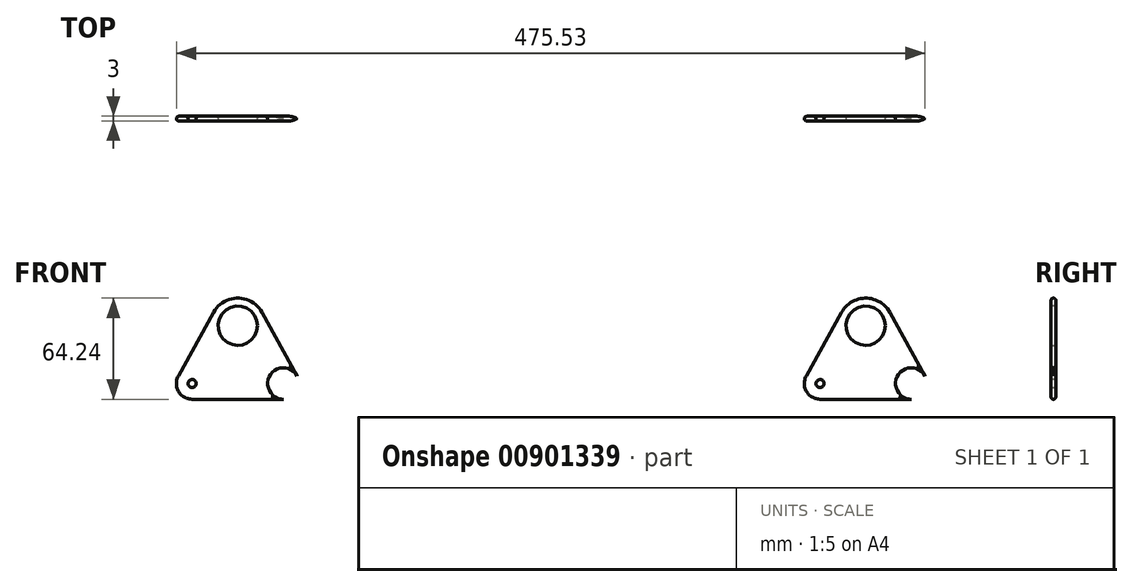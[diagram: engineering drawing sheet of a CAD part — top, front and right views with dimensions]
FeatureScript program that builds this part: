
annotation { "Feature Type Name" : "Feature", "Feature Type Description" : "" }
export const myFeature = defineFeature(function(context is Context, id is Id, definition is map)
    precondition{}
    {
        {
            var Q0;
            Q0=qCreatedBy(makeId("Front.planeOp"),FACE);
            var sketch = newSketch(context, id + "F0", { "sketchPlane" : qUnion([Q0])});
            skLineSegment(sketch, "E0", {"start": v(-199.41, 0) * mm, "end": v(-199.41, 45) * mm});
            skCircle(sketch, "E1", {"center": v(-199.41, 45) * mm, "radius": 17.5 * mm});
            skLineSegment(sketch, "E2", {"start": v(-199.41, 0) * mm, "end": v(-199.41, -45) * mm});
            skLineSegment(sketch, "E3", {"start": v(-199.41, -45) * mm, "end": v(-269.41, -45) * mm});
            skLineSegment(sketch, "E4", {"start": v(-199.41, -45) * mm, "end": v(-129.41, -45) * mm});
            skLineSegment(sketch, "E5", {"start": v(-129.41, -45) * mm, "end": v(-184.11, 53.5) * mm});
            skLineSegment(sketch, "E6", {"start": v(-269.41, -45) * mm, "end": v(-214.71, 53.5) * mm});
            skCircle(sketch, "E7", {"center": v(-239.67, -27.5) * mm, "radius": 17.5 * mm});
            skCircle(sketch, "E8", {"center": v(-159.15, -27.5) * mm, "radius": 17.5 * mm});
            skLineSegment(sketch, "E9", {"start": v(199.41, 0) * mm, "end": v(199.41, 45) * mm});
            skCircle(sketch, "E10", {"center": v(199.41, 45) * mm, "radius": 17.5 * mm});
            skLineSegment(sketch, "E11", {"start": v(199.41, 0) * mm, "end": v(199.41, -45) * mm});
            skLineSegment(sketch, "E12", {"start": v(199.41, -45) * mm, "end": v(129.41, -45) * mm});
            skLineSegment(sketch, "E13", {"start": v(199.41, -45) * mm, "end": v(269.41, -45) * mm});
            skLineSegment(sketch, "E14", {"start": v(269.41, -45) * mm, "end": v(214.71, 53.5) * mm});
            skLineSegment(sketch, "E15", {"start": v(129.41, -45) * mm, "end": v(184.11, 53.5) * mm});
            skCircle(sketch, "E16", {"center": v(159.15, -27.5) * mm, "radius": 17.5 * mm});
            skCircle(sketch, "E17", {"center": v(239.67, -27.5) * mm, "radius": 17.5 * mm});
            skCircle(sketch, "E18", {"center": v(-199.41, 45) * mm, "radius": 12.5 * mm});
            skCircle(sketch, "E19", {"center": v(199.41, 45) * mm, "radius": 12.5 * mm});
            skCircle(sketch, "E20", {"center": v(-228.4, 8.26) * mm, "radius": 10 * mm});
            skCircle(sketch, "E21.MirrorC", {"center": v(-170.43, 8.26) * mm, "radius": 10 * mm});
            skCircle(sketch, "E22.MirrorC", {"center": v(228.4, 8.26) * mm, "radius": 10 * mm});
            skCircle(sketch, "E23.MirrorC", {"center": v(170.43, 8.26) * mm, "radius": 10 * mm});
            skLineSegment(sketch, "E24", {"start": v(-228.4, -1.74) * mm, "end": v(-170.43, -1.74) * mm});
            skLineSegment(sketch, "E25.MirrorCS", {"start": v(228.4, -1.74) * mm, "end": v(170.43, -1.74) * mm});
            skCircle(sketch, "E26", {"center": v(-228.4, 8.26) * mm, "radius": 2.5 * mm});
            skCircle(sketch, "E27", {"center": v(-170.43, 8.26) * mm, "radius": 2.5 * mm});
            skCircle(sketch, "E28.MirrorC", {"center": v(170.43, 8.26) * mm, "radius": 2.5 * mm});
            skCircle(sketch, "E29.MirrorC", {"center": v(228.4, 8.26) * mm, "radius": 2.5 * mm});
            skLineSegment(sketch, "E30", {"start": v(-228.4, -1.74) * mm, "end": v(-199.41, -1.74) * mm});
            skSolve(sketch);
        }
        {
            var Q0;
            {var subQ0=sQuery(id+"F0.wireOp",EDGE,"E2");var subQ1=sQuery(id+"F0.wireOp",EDGE,"E0");var subQ2=makeQuery(id+"F0.imprint","INTERSECT",VERTEX,{"derivedFrom":[subQ1,subQ0]});Q0=makeQuery(id+"F0.imprint","IMPRINT",FACE,{"disambiguationData":[TD([[makeQuery(id+"F0.imprint","IMPRINT",EDGE,{"disambiguationData":[TD([[subQ2,-1.0]])],"derivedFrom":subQ1}),1.0]])]});}
            var Q1;
            Q1=makeQuery(id+"F0.imprint","IMPRINT",FACE,{"disambiguationData":[TD([[makeQuery(id+"F0.imprint","IMPRINT",EDGE,{"derivedFrom":sQuery(id+"F0.wireOp",EDGE,"E18")}),-1.0]])]});
            var Q2;
            {var subQ7=sQuery(id+"F0.wireOp",EDGE,"E2");var subQ8=sQuery(id+"F0.wireOp",EDGE,"E0");var subQ9=makeQuery(id+"F0.imprint","INTERSECT",VERTEX,{"derivedFrom":[subQ8,subQ7]});Q2=makeQuery(id+"F0.imprint","IMPRINT",FACE,{"disambiguationData":[TD([[makeQuery(id+"F0.imprint","IMPRINT",EDGE,{"disambiguationData":[TD([[subQ9,-1.0]])],"derivedFrom":subQ8}),-1.0]])]});}
            var Q3;
            {var subQ0=sQuery(id+"F0.wireOp",EDGE,"E11");var subQ1=sQuery(id+"F0.wireOp",EDGE,"E9");var subQ2=makeQuery(id+"F0.imprint","INTERSECT",VERTEX,{"derivedFrom":[subQ1,subQ0]});Q3=makeQuery(id+"F0.imprint","IMPRINT",FACE,{"disambiguationData":[TD([[makeQuery(id+"F0.imprint","IMPRINT",EDGE,{"disambiguationData":[TD([[subQ2,-1.0]])],"derivedFrom":subQ1}),1.0]])]});}
            var Q4;
            Q4=makeQuery(id+"F0.imprint","IMPRINT",FACE,{"disambiguationData":[TD([[makeQuery(id+"F0.imprint","IMPRINT",EDGE,{"derivedFrom":sQuery(id+"F0.wireOp",EDGE,"E19")}),-1.0]])]});
            var Q5;
            {var subQ5=sQuery(id+"F0.wireOp",EDGE,"E11");var subQ6=sQuery(id+"F0.wireOp",EDGE,"E9");var subQ7=makeQuery(id+"F0.imprint","INTERSECT",VERTEX,{"derivedFrom":[subQ6,subQ5]});Q5=makeQuery(id+"F0.imprint","IMPRINT",FACE,{"disambiguationData":[TD([[makeQuery(id+"F0.imprint","IMPRINT",EDGE,{"disambiguationData":[TD([[subQ7,-1.0]])],"derivedFrom":subQ6}),-1.0]])]});}
            var Q6;
            {var subQ0=sQuery(id+"F0.wireOp",EDGE,"E20");var subQ1=makeQuery(id+"F0.imprint","INTERSECT",VERTEX,{"derivedFrom":[subQ0,sQuery(id+"F0.wireOp",EDGE,"E24")]});Q6=makeQuery(id+"F0.imprint","IMPRINT",FACE,{"disambiguationData":[TD([[makeQuery(id+"F0.imprint","IMPRINT",EDGE,{"disambiguationData":[TD([[subQ1,1.0]])],"derivedFrom":subQ0}),1.0]])]});}
            var Q7;
            {var subQ0=sQuery(id+"F0.wireOp",EDGE,"E21.MirrorC");var subQ1=makeQuery(id+"F0.imprint","INTERSECT",VERTEX,{"derivedFrom":[subQ0,sQuery(id+"F0.wireOp",EDGE,"E24")]});Q7=makeQuery(id+"F0.imprint","IMPRINT",FACE,{"disambiguationData":[TD([[makeQuery(id+"F0.imprint","IMPRINT",EDGE,{"disambiguationData":[TD([[subQ1,1.0]])],"derivedFrom":subQ0}),-1.0]])]});}
            var Q8;
            {var subQ0=sQuery(id+"F0.wireOp",EDGE,"E23.MirrorC");var subQ1=makeQuery(id+"F0.imprint","INTERSECT",VERTEX,{"derivedFrom":[subQ0,sQuery(id+"F0.wireOp",EDGE,"E25.MirrorCS")]});Q8=makeQuery(id+"F0.imprint","IMPRINT",FACE,{"disambiguationData":[TD([[makeQuery(id+"F0.imprint","IMPRINT",EDGE,{"disambiguationData":[TD([[subQ1,1.0]])],"derivedFrom":subQ0}),1.0]])]});}
            var Q9;
            {var subQ0=sQuery(id+"F0.wireOp",EDGE,"E22.MirrorC");var subQ1=makeQuery(id+"F0.imprint","INTERSECT",VERTEX,{"derivedFrom":[subQ0,sQuery(id+"F0.wireOp",EDGE,"E25.MirrorCS")]});Q9=makeQuery(id+"F0.imprint","IMPRINT",FACE,{"disambiguationData":[TD([[makeQuery(id+"F0.imprint","IMPRINT",EDGE,{"disambiguationData":[TD([[subQ1,1.0]])],"derivedFrom":subQ0}),-1.0]])]});}
            extrude(context, id + "F1", {"entities" : qUnion([Q0, Q1, Q2, Q3, Q4, Q5, Q6, Q7, Q8, Q9]), "endBound" : BoundingType.SYMMETRIC, "depth" : 3 * mm, "offsetDistance" : 25 * mm});
        }
        {
            var Q0;
            Q0=makeQuery(id+"F1.opExtrude","CAP_FACE",FACE,{"disambiguationData":[OSD([sQuery(id+"F0.wireOp",EDGE,"E1"),sQuery(id+"F0.wireOp",EDGE,"E3"),sQuery(id+"F0.wireOp",EDGE,"E4"),sQuery(id+"F0.wireOp",EDGE,"E5"),sQuery(id+"F0.wireOp",EDGE,"E6"),sQuery(id+"F0.wireOp",EDGE,"E7"),sQuery(id+"F0.wireOp",EDGE,"E8")])],"isStart":false});
            var Q1;
            Q1=makeQuery(id+"F1.opExtrude","CAP_FACE",FACE,{"disambiguationData":[OSD([sQuery(id+"F0.wireOp",EDGE,"E10"),sQuery(id+"F0.wireOp",EDGE,"E12"),sQuery(id+"F0.wireOp",EDGE,"E13"),sQuery(id+"F0.wireOp",EDGE,"E14"),sQuery(id+"F0.wireOp",EDGE,"E15"),sQuery(id+"F0.wireOp",EDGE,"E16"),sQuery(id+"F0.wireOp",EDGE,"E17")])],"isStart":false});
            var Q2;
            Q2=makeQuery(id+"F1.opExtrude","CAP_FACE",FACE,{"disambiguationData":[OSD([sQuery(id+"F0.wireOp",EDGE,"E10"),sQuery(id+"F0.wireOp",EDGE,"E12"),sQuery(id+"F0.wireOp",EDGE,"E13"),sQuery(id+"F0.wireOp",EDGE,"E14"),sQuery(id+"F0.wireOp",EDGE,"E15"),sQuery(id+"F0.wireOp",EDGE,"E16"),sQuery(id+"F0.wireOp",EDGE,"E17")])],"isStart":true});
            var Q3;
            Q3=makeQuery(id+"F1.opExtrude","CAP_FACE",FACE,{"disambiguationData":[OSD([sQuery(id+"F0.wireOp",EDGE,"E1"),sQuery(id+"F0.wireOp",EDGE,"E3"),sQuery(id+"F0.wireOp",EDGE,"E4"),sQuery(id+"F0.wireOp",EDGE,"E5"),sQuery(id+"F0.wireOp",EDGE,"E6"),sQuery(id+"F0.wireOp",EDGE,"E7"),sQuery(id+"F0.wireOp",EDGE,"E8")])],"isStart":true});
            fillet(context, id + "F2", {"entities" : qUnion([Q0, Q1, Q2, Q3]), "radius" : 1.5 * mm, "tangentPropagation" : true, "allowEdgeOverflow" : false});
        }
    });
